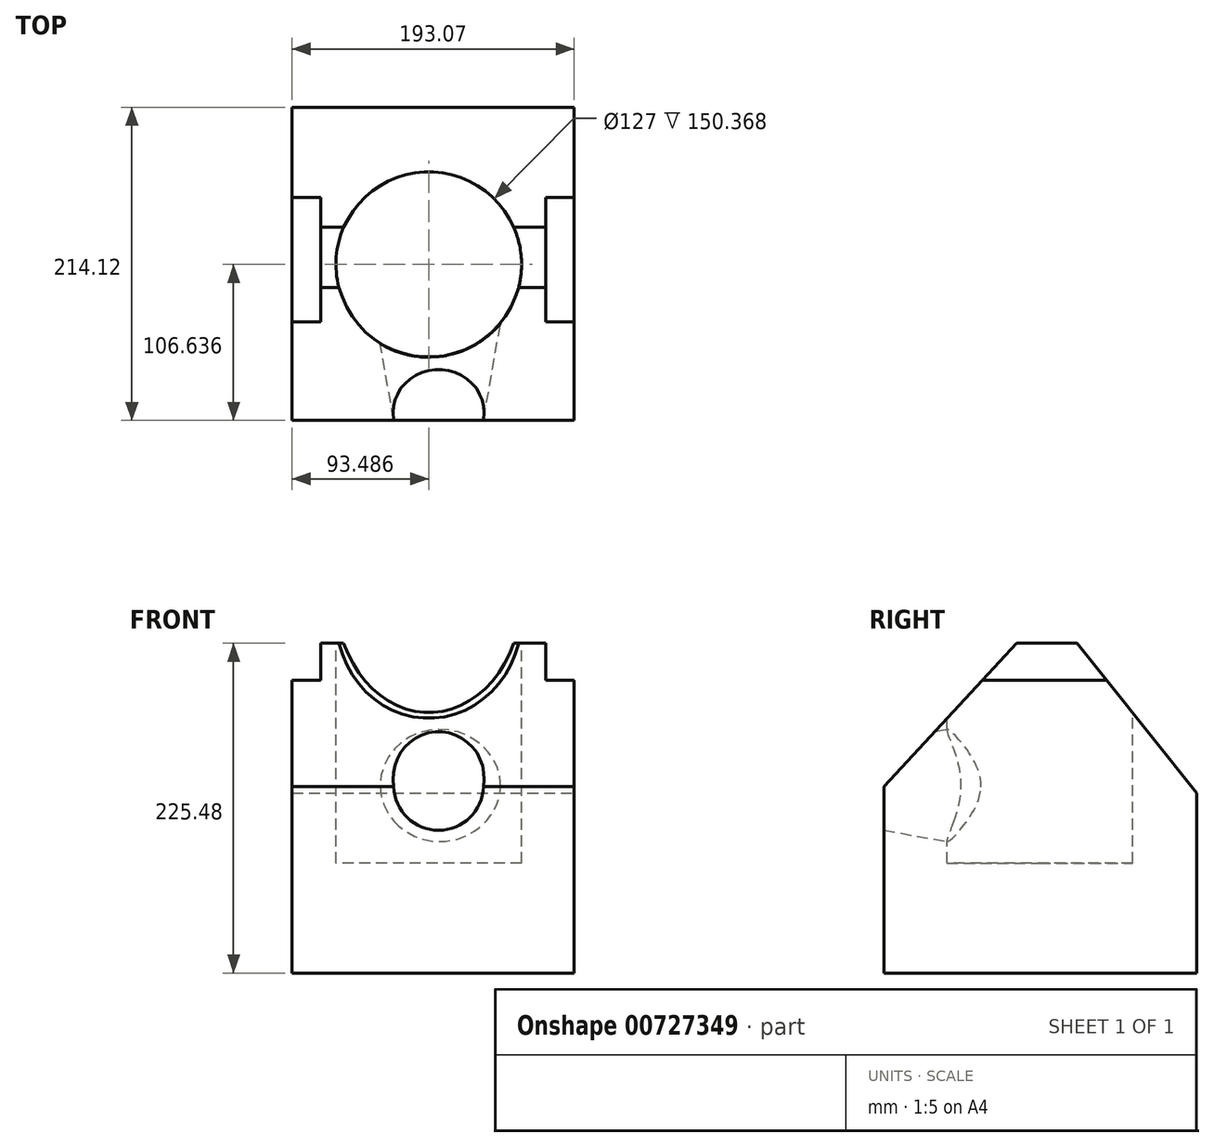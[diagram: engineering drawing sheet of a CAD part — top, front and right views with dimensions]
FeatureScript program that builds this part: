
annotation { "Feature Type Name" : "Feature", "Feature Type Description" : "" }
export const myFeature = defineFeature(function(context is Context, id is Id, definition is map)
    precondition{}
    {
        {
            var Q0;
            Q0=qCreatedBy(makeId("Front.planeOp"),FACE);
            var sketch = newSketch(context, id + "F0", { "sketchPlane" : qUnion([Q0])});
            skLineSegment(sketch, "E0.bottom", {"start": v(-100.23, 62.24) * mm, "end": v(92.84, 62.24) * mm});
            skLineSegment(sketch, "E0.top", {"start": v(-100.23, -137.84) * mm, "end": v(92.84, -137.84) * mm});
            skLineSegment(sketch, "E0.left", {"start": v(-100.23, 62.24) * mm, "end": v(-100.23, -137.84) * mm});
            skLineSegment(sketch, "E0.right", {"start": v(92.84, 62.24) * mm, "end": v(92.84, -137.84) * mm});
            skSolve(sketch);
        }
        {
            var Q0;
            Q0 = qSketchRegion(id + "F0", true);
            extrude(context, id + "F1", {"entities" : qUnion([Q0]), "depth" : 214.12 * mm, "offsetDistance" : 25.4 * mm});
        }
        {
            var Q0;
            Q0=makeQuery(id+"F1.opExtrude","SWEPT_FACE",FACE,{"disambiguationData":[OSD([sQuery(id+"F0.wireOp",EDGE,"E0.bottom")])]});
            var sketch = newSketch(context, id + "F2", { "sketchPlane" : qUnion([Q0])});
            skLineSegment(sketch, "E1.0", {"start": v(73.28, -19.56) * mm, "end": v(-80.67, -19.56) * mm});
            skLineSegment(sketch, "E1.1", {"start": v(73.28, -194.56) * mm, "end": v(73.28, -19.56) * mm});
            skLineSegment(sketch, "E1.2", {"start": v(-80.67, -194.56) * mm, "end": v(73.28, -194.56) * mm});
            skLineSegment(sketch, "E1.3", {"start": v(-80.67, -19.56) * mm, "end": v(-80.67, -194.56) * mm});
            skSolve(sketch);
        }
        {
            var Q0;
            Q0=makeQuery(id+"F2.imprint","IMPRINT",FACE,{"disambiguationData":[TD([[makeQuery(id+"F2.imprint","IMPRINT",EDGE,{"derivedFrom":sQuery(id+"F2.wireOp",EDGE,"E1.0")}),1.0]])]});
            extrude(context, id + "F3", {"entities" : qUnion([Q0]), "operationType" : NewBodyOperationType.ADD, "depth" : 25.4 * mm, "offsetDistance" : 25.4 * mm});
        }
        {
            var Q0;
            Q0=makeQuery(id+"F3.opExtrude","CAP_FACE",FACE,{"disambiguationData":[OSD([sQuery(id+"F2.wireOp",EDGE,"E1.0"),sQuery(id+"F2.wireOp",EDGE,"E1.1"),sQuery(id+"F2.wireOp",EDGE,"E1.2"),sQuery(id+"F2.wireOp",EDGE,"E1.3")])],"isStart":false});
            var sketch = newSketch(context, id + "F4", { "sketchPlane" : qUnion([Q0])});
            skCircle(sketch, "E2", {"center": v(-6.74, -107.48) * mm, "radius": 63.5 * mm});
            skSolve(sketch);
        }
        {
            var Q0;
            Q0=makeQuery(id+"F4.imprint","IMPRINT",FACE,{"disambiguationData":[TD([[makeQuery(id+"F4.imprint","IMPRINT",EDGE,{"derivedFrom":sQuery(id+"F4.wireOp",EDGE,"E2")}),1.0]])]});
            extrude(context, id + "F5", {"entities" : qUnion([Q0]), "operationType" : NewBodyOperationType.REMOVE, "oppositeDirection" : true, "depth" : 150.37 * mm, "offsetDistance" : 25.4 * mm});
        }
        {
            var Q0;
            Q0=makeQuery(id+"F1.opExtrude","CAP_FACE",FACE,{"disambiguationData":[OSD([sQuery(id+"F0.wireOp",EDGE,"E0.bottom"),sQuery(id+"F0.wireOp",EDGE,"E0.top"),sQuery(id+"F0.wireOp",EDGE,"E0.left"),sQuery(id+"F0.wireOp",EDGE,"E0.right")])],"isStart":false});
            var sketch = newSketch(context, id + "F6", { "sketchPlane" : qUnion([Q0])});
            skCircle(sketch, "E3", {"center": v(0, -9.51) * mm, "radius": 30.7 * mm});
            skSolve(sketch);
        }
        {
            var Q0;
            Q0 = qSketchRegion(id + "F6", true);
            extrude(context, id + "F7", {"entities" : qUnion([Q0]), "operationType" : NewBodyOperationType.REMOVE, "oppositeDirection" : true, "depth" : 70.61 * mm, "offsetDistance" : 25.4 * mm, "hasDraft" : true, "draftAngle" : 10 * degree});
        }
        {
            var Q0;
            Q0=makeQuery(id+"F1.opExtrude","SWEPT_FACE",FACE,{"disambiguationData":[OSD([sQuery(id+"F0.wireOp",EDGE,"E0.right")])]});
            var sketch = newSketch(context, id + "F8", { "sketchPlane" : qUnion([Q0])});
            skLineSegment(sketch, "E4", {"start": v(-214.12, -10.33) * mm, "end": v(-214.12, 62.24) * mm});
            skLineSegment(sketch, "E5", {"start": v(-214.12, 62.24) * mm, "end": v(-194.47, 123.28) * mm});
            skLineSegment(sketch, "E6", {"start": v(-194.47, 123.28) * mm, "end": v(-90.17, 123.28) * mm});
            skLineSegment(sketch, "E7", {"start": v(-90.17, 123.28) * mm, "end": v(-214.12, -10.33) * mm});
            skSolve(sketch);
        }
        {
            var Q0;
            Q0 = qSketchRegion(id + "F8", true);
            extrude(context, id + "F9", {"entities" : qUnion([Q0]), "operationType" : NewBodyOperationType.REMOVE, "oppositeDirection" : true, "depth" : 366.78 * mm, "offsetDistance" : 25.4 * mm});
        }
        {
            var Q0;
            Q0=makeQuery(id+"F1.opExtrude","SWEPT_FACE",FACE,{"disambiguationData":[OSD([sQuery(id+"F0.wireOp",EDGE,"E0.right")])]});
            var sketch = newSketch(context, id + "F10", { "sketchPlane" : qUnion([Q0])});
            skLineSegment(sketch, "E8", {"start": v(0, -14.8) * mm, "end": v(0, 62.24) * mm});
            skLineSegment(sketch, "E9", {"start": v(0, 62.24) * mm, "end": v(-34.74, 118.6) * mm});
            skLineSegment(sketch, "E10", {"start": v(-34.74, 118.6) * mm, "end": v(-93.46, 101.81) * mm});
            skLineSegment(sketch, "E11", {"start": v(-93.46, 101.81) * mm, "end": v(0, -14.8) * mm});
            skSolve(sketch);
        }
        {
            var Q0;
            Q0 = qSketchRegion(id + "F10", true);
            extrude(context, id + "F11", {"entities" : qUnion([Q0]), "operationType" : NewBodyOperationType.REMOVE, "endBound" : BoundingType.THROUGH_ALL, "oppositeDirection" : true, "depth" : 25.4 * mm, "offsetDistance" : 25.4 * mm});
        }
    });
